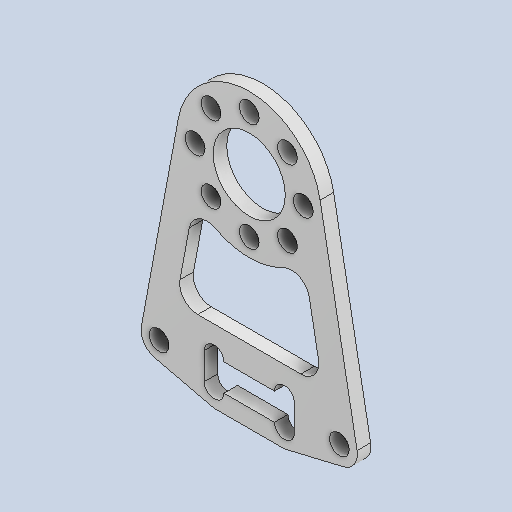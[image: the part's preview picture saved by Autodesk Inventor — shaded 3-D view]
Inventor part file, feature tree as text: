
AUTODESK INVENTOR PART (.ipt)
format: ipt  version: 2025.1 (Build 291241000, 241)  size: 239,104 bytes
history: native  units: mm
features: other x5, extrude x2, sketch x2, fillet x1, reference x1
ambient origin geometry x8: Origin, YZ Plane, XZ Plane, XY Plane, X Axis, Y Axis, Z Axis, Center Point
bodies: Body1 (feature_tree)
feature tree (11):
  other  "ソリッド1"
  extrude  "押し出し1"  Depth=8.0mm
  extrude  "押し出し2"  Depth=16.0mm
  fillet  "フィレット1"  Radius=12.0mm
  sketch  "スケッチ1"
  other  "スケッチ円形状パターン1"
  reference  "参照1"
  sketch  "スケッチ2"
  other  "<userpath>\Documents\Inventor\Vixen\doutai.iam"
  other  "doutai.iam"
  other  "KRS2500_scale:7"
